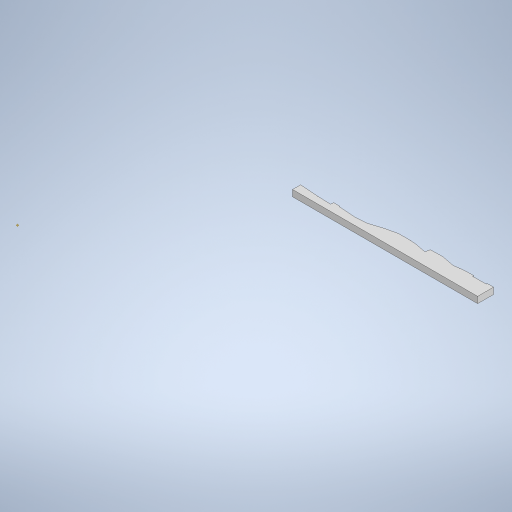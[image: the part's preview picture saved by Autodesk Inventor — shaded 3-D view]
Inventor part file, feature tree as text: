
AUTODESK INVENTOR PART (.ipt)
format: ipt  version: 2023 (Build 270158000, 158)  size: 5,538,816 bytes
history: native  units: mm
features: sketch x2, extrude x1, other x1
ambient origin geometry x8: Origin, YZ Plane, XZ Plane, XY Plane, X Axis, Y Axis, Z Axis, Center Point
bodies: Body1 (feature_tree)
feature tree (4):
  sketch  "Sketch2"  dims[d29=59.42mm d30=13.56mm]
  extrude  "Extrusion5"  Depth=13.56mm
  sketch  "Sketch4"  dims[d31=8.85mm d32=8.06mm d33=9.16mm d35=10.67mm d36=8.56mm d37=8.03mm d38=6.54mm d39=10.41mm d40=7.01mm d41=11.97mm d42=11.35mm d43=6.73mm d44=12.88mm d45=4.91mm d46=12.83mm d47=11.47mm d48=12.63mm d49=6.69mm d50=3.2mm d51=1.6mm d52=14.53mm d53=3.6mm d121=2.0mm d122=0.0mm]
  other  "Image3"
